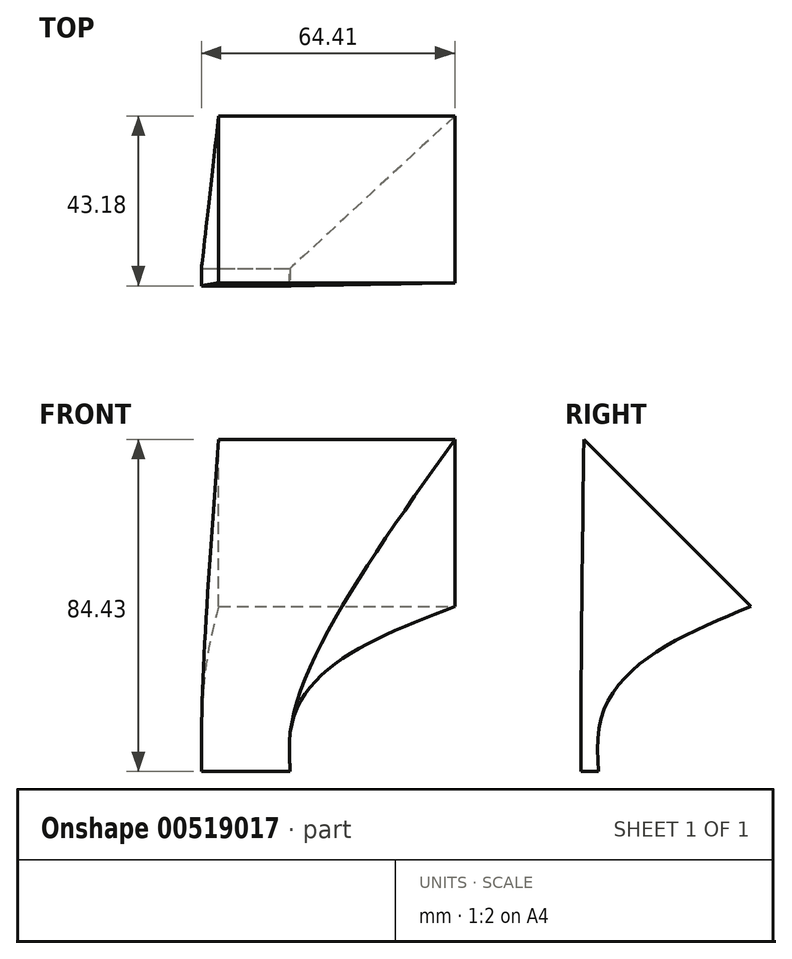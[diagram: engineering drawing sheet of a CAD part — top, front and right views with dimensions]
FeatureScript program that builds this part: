
annotation { "Feature Type Name" : "Feature", "Feature Type Description" : "" }
export const myFeature = defineFeature(function(context is Context, id is Id, definition is map)
    precondition{}
    {
        {
            var Q0;
            Q0=qCreatedBy(makeId("Top.planeOp"),FACE);
            var sketch = newSketch(context, id + "F0", { "sketchPlane" : qUnion([Q0])});
            skCircle(sketch, "E0", {"center": v(0, 0) * mm, "radius": 2.25 * mm});
            skCircle(sketch, "E1", {"center": v(-43, 38) * mm, "radius": 2.25 * mm});
            skSolve(sketch);
        }
        {
            var Q0;
            Q0=qCreatedBy(makeId("Top.planeOp"),FACE);
            var sketch = newSketch(context, id + "F1", { "sketchPlane" : qUnion([Q0])});
            skLineSegment(sketch, "E2.bottom", {"start": v(-50.39, 2.26) * mm, "end": v(-27.83, 2.26) * mm});
            skLineSegment(sketch, "E2.top", {"start": v(-50.39, -2.18) * mm, "end": v(-27.83, -2.18) * mm});
            skLineSegment(sketch, "E2.left", {"start": v(-50.39, 2.26) * mm, "end": v(-50.39, -2.18) * mm});
            skLineSegment(sketch, "E2.right", {"start": v(-27.83, 2.26) * mm, "end": v(-27.83, -2.18) * mm});
            skSolve(sketch);
        }
        {
            var Q0;
            Q0=qCreatedBy(makeId("Top.planeOp"),FACE);
            cPlane(context, id + "F2", {"entities" : qUnion([Q0]), "cplaneType" : CPlaneType.OFFSET, "offset" : 42 * mm, "width" : 150 * mm, "height" : 150 * mm});
        }
        {
            var Q0;
            Q0=qCreatedBy(makeId("Front.planeOp"),FACE);
            cPlane(context, id + "F3", {"entities" : qUnion([Q0]), "cplaneType" : CPlaneType.OFFSET, "offset" : 41 * mm, "oppositeDirection" : true, "width" : 150 * mm, "height" : 150 * mm});
        }
        {
            var Q0;
            Q0=qCreatedBy(id+"F2.planeOp",FACE);
            var sketch = newSketch(context, id + "F4", { "sketchPlane" : qUnion([Q0])});
            skLineSegment(sketch, "E3", {"start": v(-69.45, 41) * mm, "end": v(5.55, 41) * mm});
            skSolve(sketch);
        }
        {
            var Q0;
            Q0=sQuery(id+"F4.wireOp",EDGE,"E3");
            cPlane(context, id + "F5", {"entities" : qUnion([Q0]), "cplaneType" : CPlaneType.LINE_ANGLE, "offset" : 25 * mm, "angle" : 45 * degree, "width" : 150 * mm, "height" : 150 * mm});
        }
        {
            var Q0;
            Q0=qCreatedBy(id+"F5.planeOp",FACE);
            var sketch = newSketch(context, id + "F6", { "sketchPlane" : qUnion([Q0])});
            skLineSegment(sketch, "E4.top", {"start": v(46, 60.7) * mm, "end": v(-14, 60.7) * mm});
            skLineSegment(sketch, "E4.left", {"start": v(46, 0.7) * mm, "end": v(46, 60.7) * mm});
            skLineSegment(sketch, "E4.right", {"start": v(-14, 0.7) * mm, "end": v(-14, 60.7) * mm});
            skPoint(sketch, "E5.orphan", {"position": v(69.45, 0.7) * mm});
            skPoint(sketch, "E6.0.end.orphan", {"position": v(-5.55, 0.7) * mm});
            skLineSegment(sketch, "E7", {"start": v(46, 0.7) * mm, "end": v(-14, 0.7) * mm});
            skSolve(sketch);
        }
        {
            var Q0;
            Q0=qCreatedBy(makeId("Top.planeOp"),FACE);
            cPlane(context, id + "F7", {"entities" : qUnion([Q0]), "cplaneType" : CPlaneType.OFFSET, "offset" : 10 * mm, "width" : 150 * mm, "height" : 150 * mm});
        }
        {
            var Q0;
            Q0=qCreatedBy(id+"F7.planeOp",FACE);
            var sketch = newSketch(context, id + "F8", { "sketchPlane" : qUnion([Q0])});
            skLineSegment(sketch, "E8.0", {"start": v(-50.39, 2.26) * mm, "end": v(-27.83, 2.26) * mm});
            skLineSegment(sketch, "E9.0", {"start": v(-50.39, 2.26) * mm, "end": v(-50.39, -2.18) * mm});
            skLineSegment(sketch, "E10.0", {"start": v(-50.39, -2.18) * mm, "end": v(-27.83, -2.18) * mm});
            skLineSegment(sketch, "E11.0", {"start": v(-27.83, 2.26) * mm, "end": v(-27.83, -2.18) * mm});
            skSolve(sketch);
        }
        {
            var Q0;
            Q0=makeQuery(id+"F6.imprint","IMPRINT",FACE,{"disambiguationData":[TD([[makeQuery(id+"F6.imprint","IMPRINT",EDGE,{"derivedFrom":sQuery(id+"F6.wireOp",EDGE,"E4.top")}),1.0]])]});
            var Q1;
            Q1=makeQuery(id+"F8.imprint","IMPRINT",FACE,{"disambiguationData":[TD([[makeQuery(id+"F8.imprint","IMPRINT",EDGE,{"derivedFrom":sQuery(id+"F8.wireOp",EDGE,"E8.0")}),-1.0]])]});
            var Q2;
            Q2=makeQuery(id+"F1.imprint","IMPRINT",FACE,{"disambiguationData":[TD([[makeQuery(id+"F1.imprint","IMPRINT",EDGE,{"derivedFrom":sQuery(id+"F1.wireOp",EDGE,"E2.bottom")}),-1.0]])]});
            loft(context, id + "F9", {"sheetProfilesArray" : [{ "sheetProfileEntities" : qUnion([Q0]) }, { "sheetProfileEntities" : qUnion([Q1]) }, { "sheetProfileEntities" : qUnion([Q2]) }]});
        }
    });
